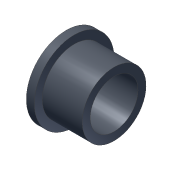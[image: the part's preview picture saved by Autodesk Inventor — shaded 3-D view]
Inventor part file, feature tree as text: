
AUTODESK INVENTOR PART (.ipt)
format: ipt  version: 2012 (Build 160160000, 160)  size: 92,672 bytes
history: native  units: in
note: dims shown in document units (in); Inventor stores cm internally (conversion verified against a paired STEP export)
features: revolve x1, sketch x1
ambient origin geometry x8: Origin, YZ Plane, XZ Plane, XY Plane, X Axis, Y Axis, Z Axis, Center Point
bodies: Solid1 (feature_tree)
feature tree (2):
  revolve  "Revolution1"  [1 undecoded]
  sketch  "Sketch1"  dims[d0=0.1875in d1=0.25in d2=0.3125in d3=0.0625in d4=0.375in d5=90.0deg]
note: 1 required parameter value undecoded (feature->parameter linkage not recoverable at this tier; creation-order binding heuristic only, values carry confidence <= 0.55)
